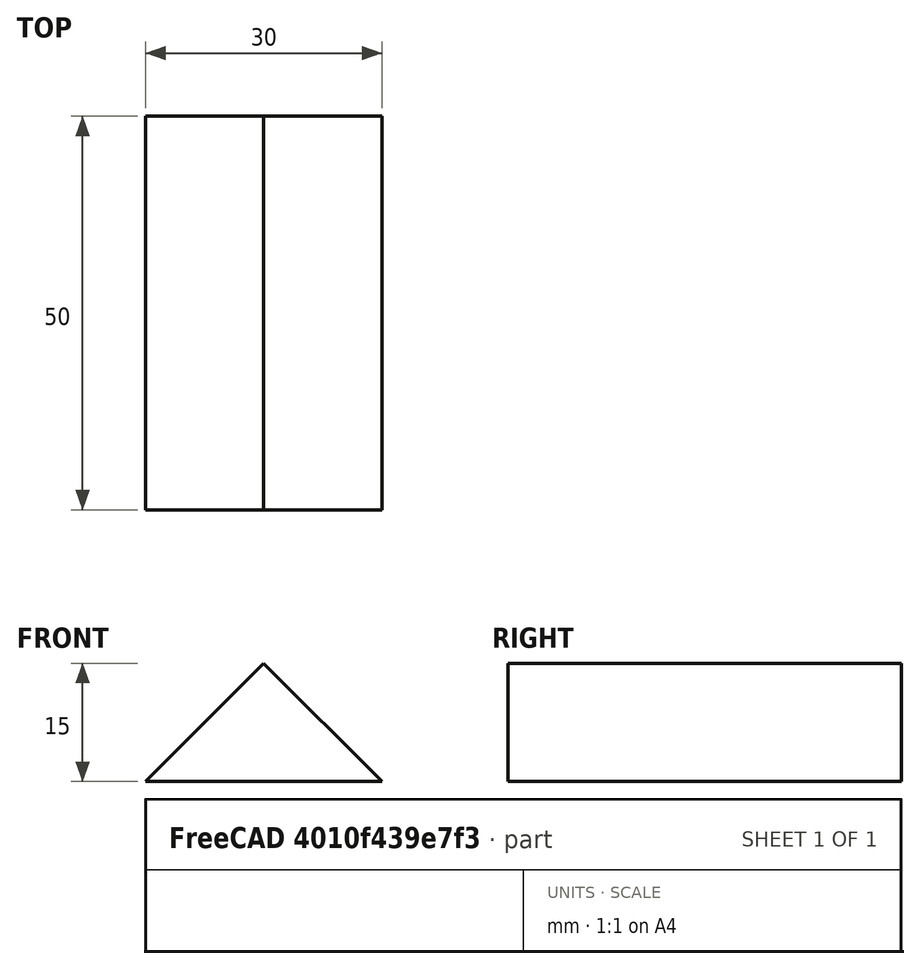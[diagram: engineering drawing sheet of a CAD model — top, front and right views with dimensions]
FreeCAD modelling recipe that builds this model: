
FCSTD DOCUMENT  (FreeCAD 0.20R29410 (Git))
Label: primsa_triang
License: Creative Commons Attribution
LicenseURL: http://creativecommons.org/licenses/by/4.0/
objects: Sketcher::SketchObject×1, Part::Extrusion×1
note: 2 computed .brp shape members not serialized (recipe doc carries the construction recipe); baked Part::Feature solids carry a one-line shape summary decoded from their .brp

FEATURE [Sketcher::SketchObject] Sketch
  FullyConstrained = true
  Placement = pos=(0,0,0) rot=(1,0,0;1.5708rad)
  sketch-geometry (3):
    g0: LineSegment StartX=-15 StartY=0 StartZ=0 EndX=0 EndY=15 EndZ=0
    g1: LineSegment StartX=0 StartY=15 StartZ=0 EndX=15 EndY=0 EndZ=0
    g2: LineSegment StartX=15 StartY=0 StartZ=0 EndX=-15 EndY=0 EndZ=0
  constraints (9):
    c: PointOnObject(g0,g-1)
    c: PointOnObject(g0,g-2)
    c: Coincident(g0,g1)
    c: PointOnObject(g1,g-1)
    c: Coincident(g1,g2)
    c: Coincident(g2,g0)
    c: Angle(g2,g0) = 0.785398
    c: DistanceX(g2,g2) = 30
    c: Angle(g1,g2) = 0.785398
FEATURE [Part::Extrusion] Extrude
  Base = -> Sketch
  Dir = (0,-1,-3e-16)
  DirMode = 2
  FaceMakerClass = Part::FaceMakerBullseye
  LengthFwd = 50
  LengthRev = 0
  Reversed = true
  Solid = true
  Symmetric = false
